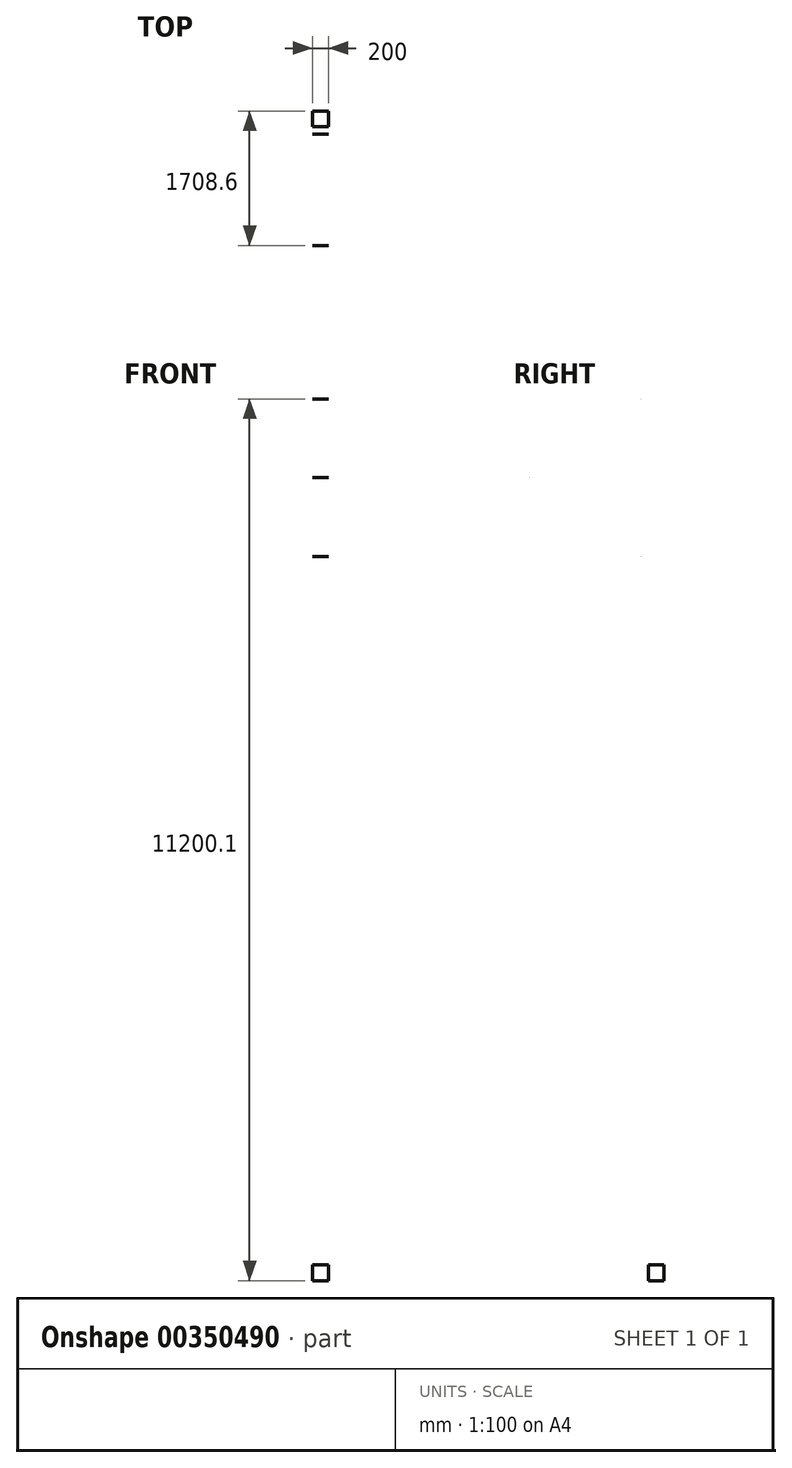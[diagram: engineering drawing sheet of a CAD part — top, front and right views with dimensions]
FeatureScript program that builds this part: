
annotation { "Feature Type Name" : "Feature", "Feature Type Description" : "" }
export const myFeature = defineFeature(function(context is Context, id is Id, definition is map)
    precondition{}
    {
        {
            var Q0;
            Q0=qCreatedBy(makeId("Right.planeOp"),FACE);
            var sketch = newSketch(context, id + "F0", { "sketchPlane" : qUnion([Q0])});
            skLineSegment(sketch, "E0", {"start": v(0, 0) * mm, "end": v(1000, 0) * mm});
            skLineSegment(sketch, "E1", {"start": v(1000, 0) * mm, "end": v(1000, 20000) * mm});
            skLineSegment(sketch, "E2", {"start": v(1000, 20000) * mm, "end": v(-1000, 20000) * mm});
            skLineSegment(sketch, "E3", {"start": v(-1000, 20000) * mm, "end": v(-1000, 0) * mm});
            skLineSegment(sketch, "E4", {"start": v(-1000, 0) * mm, "end": v(0, 0) * mm});
            skLineSegment(sketch, "E5", {"start": v(1000, 0) * mm, "end": v(800, 0) * mm});
            skLineSegment(sketch, "E6", {"start": v(800, 0) * mm, "end": v(800, 1141.07) * mm});
            skLineSegment(sketch, "E7", {"start": v(1000, 0) * mm, "end": v(1000, 200) * mm});
            skLineSegment(sketch, "E8", {"start": v(1000, 200) * mm, "end": v(-708.48, 200) * mm});
            skLineSegment(sketch, "E9", {"start": v(-1000, 0) * mm, "end": v(-800, 0) * mm});
            skLineSegment(sketch, "E10", {"start": v(-1000, 20000) * mm, "end": v(-1000, 19800) * mm});
            skLineSegment(sketch, "E11", {"start": v(800, 1141.07) * mm, "end": v(800, 200) * mm});
            skLineSegment(sketch, "E12", {"start": v(800, 1258.93) * mm, "end": v(800, 2150) * mm});
            skLineSegment(sketch, "E13", {"start": v(800, 2250) * mm, "end": v(800, 3141.07) * mm});
            skLineSegment(sketch, "E14", {"start": v(800, 3258.93) * mm, "end": v(800, 4150) * mm});
            skLineSegment(sketch, "E15", {"start": v(800, 4250) * mm, "end": v(800, 5141.07) * mm});
            skLineSegment(sketch, "E16", {"start": v(800, 5258.93) * mm, "end": v(800, 6150) * mm});
            skLineSegment(sketch, "E17", {"start": v(800, 6250) * mm, "end": v(800, 7141.07) * mm});
            skLineSegment(sketch, "E18", {"start": v(800, 7258.93) * mm, "end": v(800, 8150) * mm});
            skLineSegment(sketch, "E19", {"start": v(800, 8250) * mm, "end": v(800, 9141.07) * mm});
            skLineSegment(sketch, "E20", {"start": v(800, 9259) * mm, "end": v(800, 10150) * mm});
            skLineSegment(sketch, "E21", {"start": v(800, 10250) * mm, "end": v(800, 11141.14) * mm});
            skLineSegment(sketch, "E22", {"start": v(800, 11258.93) * mm, "end": v(800, 12150) * mm});
            skLineSegment(sketch, "E23", {"start": v(800, 12250) * mm, "end": v(800, 13141.07) * mm});
            skLineSegment(sketch, "E24", {"start": v(800, 13258.93) * mm, "end": v(800, 14150) * mm});
            skLineSegment(sketch, "E25", {"start": v(800, 14250) * mm, "end": v(800, 15141.07) * mm});
            skLineSegment(sketch, "E26", {"start": v(800, 15258.93) * mm, "end": v(800, 16150) * mm});
            skLineSegment(sketch, "E27", {"start": v(800, 16250) * mm, "end": v(800, 17141.07) * mm});
            skLineSegment(sketch, "E28", {"start": v(800, 17258.93) * mm, "end": v(800, 18150) * mm});
            skLineSegment(sketch, "E29", {"start": v(800, 18250) * mm, "end": v(800, 19141.07) * mm});
            skLineSegment(sketch, "E30", {"start": v(800, 19253.39) * mm, "end": v(800, 19800) * mm});
            skLineSegment(sketch, "E31", {"start": v(705.7, 9200) * mm, "end": v(705.4, 9200) * mm});
            skLineSegment(sketch, "E32", {"start": v(-708.6, 10204.1) * mm, "end": v(-708.37, 10204.1) * mm});
            skLineSegment(sketch, "E33", {"start": v(705.54, 11200) * mm, "end": v(705.24, 11200) * mm});
            skLineSegment(sketch, "E34", {"start": v(-803.08, 19800) * mm, "end": v(-802.95, 19800) * mm});
            skLineSegment(sketch, "E35.0.right", {"start": v(800, 19253.39) * mm, "end": v(-660.32, 19800) * mm});
            skArc(sketch, "E36.0.endCap", {"start": v(-802.95, 19150) * mm, "mid": v(-803.02, 19150) * mm, "end": v(-803.08, 19150) * mm});
            skArc(sketch, "E37.0.startCap", {"start": v(-802.95, 18150) * mm, "mid": v(-803.02, 18150) * mm, "end": v(-803.08, 18150) * mm});
            skLineSegment(sketch, "E37.0.left", {"start": v(-803.08, 18258.85) * mm, "end": v(625.39, 19150) * mm});
            skArc(sketch, "E37.1.endCap", {"start": v(-802.95, 18150) * mm, "mid": v(-803.02, 18150) * mm, "end": v(-803.08, 18150) * mm});
            skLineSegment(sketch, "E37.1.left", {"start": v(800, 18150) * mm, "end": v(-628.34, 18150) * mm});
            skLineSegment(sketch, "E37.1.right", {"start": v(800, 18250) * mm, "end": v(-628.34, 18250) * mm});
            skLineSegment(sketch, "E37.2.right", {"start": v(800, 17258.93) * mm, "end": v(-628.34, 18150) * mm});
            skArc(sketch, "E37.3.endCap", {"start": v(-802.95, 17150) * mm, "mid": v(-803.02, 17150) * mm, "end": v(-803.08, 17150) * mm});
            skArc(sketch, "E37.4.startCap", {"start": v(-802.95, 16150) * mm, "mid": v(-803.02, 16150) * mm, "end": v(-803.08, 16150) * mm});
            skLineSegment(sketch, "E37.4.left", {"start": v(-803.08, 16258.85) * mm, "end": v(625.39, 17150) * mm});
            skArc(sketch, "E37.5.endCap", {"start": v(-802.95, 16150) * mm, "mid": v(-803.02, 16150) * mm, "end": v(-803.08, 16150) * mm});
            skLineSegment(sketch, "E37.5.left", {"start": v(800, 16150) * mm, "end": v(-628.34, 16150) * mm});
            skLineSegment(sketch, "E37.5.right", {"start": v(800, 16250) * mm, "end": v(-628.34, 16250) * mm});
            skLineSegment(sketch, "E37.6.right", {"start": v(800, 15258.93) * mm, "end": v(-628.34, 16150) * mm});
            skArc(sketch, "E37.7.endCap", {"start": v(-802.95, 15150) * mm, "mid": v(-803.02, 15150) * mm, "end": v(-803.08, 15150) * mm});
            skArc(sketch, "E37.8.startCap", {"start": v(-802.95, 14150) * mm, "mid": v(-803.02, 14150) * mm, "end": v(-803.08, 14150) * mm});
            skLineSegment(sketch, "E37.8.left", {"start": v(-803.08, 14258.85) * mm, "end": v(625.39, 15150) * mm});
            skArc(sketch, "E37.9.endCap", {"start": v(-802.95, 14150) * mm, "mid": v(-803.02, 14150) * mm, "end": v(-803.08, 14150) * mm});
            skLineSegment(sketch, "E37.9.left", {"start": v(800, 14150) * mm, "end": v(-628.34, 14150) * mm});
            skLineSegment(sketch, "E37.9.right", {"start": v(800, 14250) * mm, "end": v(-628.34, 14250) * mm});
            skLineSegment(sketch, "E37.10.right", {"start": v(800, 13258.93) * mm, "end": v(-628.34, 14150) * mm});
            skArc(sketch, "E37.11.endCap", {"start": v(-802.95, 13150) * mm, "mid": v(-803.02, 13150) * mm, "end": v(-803.08, 13150) * mm});
            skArc(sketch, "E37.12.startCap", {"start": v(-802.95, 12150) * mm, "mid": v(-803.02, 12150) * mm, "end": v(-803.08, 12150) * mm});
            skLineSegment(sketch, "E37.12.left", {"start": v(-803.08, 12258.85) * mm, "end": v(625.39, 13150) * mm});
            skArc(sketch, "E37.13.endCap", {"start": v(-802.95, 12150) * mm, "mid": v(-803.02, 12150) * mm, "end": v(-803.08, 12150) * mm});
            skLineSegment(sketch, "E37.13.left", {"start": v(800, 12150) * mm, "end": v(-628.34, 12150) * mm});
            skLineSegment(sketch, "E37.13.right", {"start": v(800, 12250) * mm, "end": v(-628.34, 12250) * mm});
            skLineSegment(sketch, "E37.14.right", {"start": v(800, 11258.93) * mm, "end": v(-628.34, 12150) * mm});
            skArc(sketch, "E37.15.endCap", {"start": v(-802.95, 11150) * mm, "mid": v(-803.02, 11150) * mm, "end": v(-803.08, 11150) * mm});
            skLineSegment(sketch, "E37.16.left", {"start": v(-803.08, 10263.13) * mm, "end": v(624.74, 11150) * mm});
            skArc(sketch, "E37.17.endCap", {"start": v(800, 10150) * mm, "mid": v(799.93, 10150) * mm, "end": v(799.86, 10150) * mm});
            skLineSegment(sketch, "E37.17.right", {"start": v(-803.08, 10154.35) * mm, "end": v(-803.08, 10154.35) * mm});
            skLineSegment(sketch, "E37.18.right", {"start": v(800, 9259) * mm, "end": v(-628.22, 10153.88) * mm});
            skLineSegment(sketch, "E37.19.right", {"start": v(626.03, 9250) * mm, "end": v(-803.08, 9250) * mm});
            skLineSegment(sketch, "E37.20.left", {"start": v(-803.08, 8258.93) * mm, "end": v(625.25, 9150) * mm});
            skLineSegment(sketch, "E37.21.left", {"start": v(800, 8150) * mm, "end": v(-628.34, 8150) * mm});
            skLineSegment(sketch, "E37.21.right", {"start": v(800, 8250) * mm, "end": v(-628.34, 8250) * mm});
            skLineSegment(sketch, "E37.22.right", {"start": v(800, 7258.93) * mm, "end": v(-628.34, 8150) * mm});
            skLineSegment(sketch, "E37.23.left", {"start": v(625.25, 7150) * mm, "end": v(-803.08, 7150) * mm});
            skLineSegment(sketch, "E37.23.right", {"start": v(625.25, 7250) * mm, "end": v(-803.08, 7250) * mm});
            skLineSegment(sketch, "E37.24.left", {"start": v(-803.08, 6258.93) * mm, "end": v(625.25, 7150) * mm});
            skLineSegment(sketch, "E37.25.left", {"start": v(800, 6150) * mm, "end": v(-628.34, 6150) * mm});
            skLineSegment(sketch, "E37.25.right", {"start": v(800, 6250) * mm, "end": v(-628.34, 6250) * mm});
            skLineSegment(sketch, "E37.26.right", {"start": v(800, 5258.93) * mm, "end": v(-628.34, 6150) * mm});
            skLineSegment(sketch, "E37.28.left", {"start": v(-803.08, 4258.93) * mm, "end": v(625.25, 5150) * mm});
            skLineSegment(sketch, "E37.29.left", {"start": v(800, 4150) * mm, "end": v(-628.34, 4150) * mm});
            skLineSegment(sketch, "E37.29.right", {"start": v(800, 4250) * mm, "end": v(-628.34, 4250) * mm});
            skLineSegment(sketch, "E37.30.right", {"start": v(800, 3258.93) * mm, "end": v(-628.34, 4150) * mm});
            skLineSegment(sketch, "E37.31.right", {"start": v(625.25, 3250) * mm, "end": v(-803.08, 3250) * mm});
            skLineSegment(sketch, "E37.32.left", {"start": v(-803.08, 2258.93) * mm, "end": v(625.25, 3150) * mm});
            skLineSegment(sketch, "E37.33.left", {"start": v(800, 2150) * mm, "end": v(-628.34, 2150) * mm});
            skLineSegment(sketch, "E37.33.right", {"start": v(800, 2250) * mm, "end": v(-628.34, 2250) * mm});
            skLineSegment(sketch, "E37.34.right", {"start": v(800, 1258.93) * mm, "end": v(-628.34, 2150) * mm});
            skLineSegment(sketch, "E37.36.left", {"start": v(800, 1141.07) * mm, "end": v(-708.48, 200) * mm});
            skLineSegment(sketch, "E37.36.right", {"start": v(625.39, 1150) * mm, "end": v(-802.95, 258.93) * mm});
            skLineSegment(sketch, "E38.trimOffspring", {"start": v(625.25, 1250) * mm, "end": v(-803.08, 2141.07) * mm});
            skLineSegment(sketch, "E39.trimOffspring", {"start": v(625.25, 1250) * mm, "end": v(-803.08, 1250) * mm});
            skLineSegment(sketch, "E40.trimOffspring", {"start": v(625.39, 1150) * mm, "end": v(-802.95, 1150) * mm});
            skPoint(sketch, "E37.35.endCap.center.orphan", {"position": v(-803.08, 1200) * mm});
            skLineSegment(sketch, "E41.trimOffspring", {"start": v(-803.08, 1250) * mm, "end": v(-803.08, 2141.07) * mm});
            skLineSegment(sketch, "E42.trimOffspring", {"start": v(-802.95, 258.93) * mm, "end": v(-802.95, 1150) * mm});
            skPoint(sketch, "E43.orphan", {"position": v(-803.08, 200) * mm});
            skLineSegment(sketch, "E44.trimOffspring", {"start": v(-628.34, 2250) * mm, "end": v(800, 3141.07) * mm});
            skLineSegment(sketch, "E45.trimOffspring", {"start": v(-803.08, 2258.93) * mm, "end": v(-803.08, 3150) * mm});
            skPoint(sketch, "E37.33.endCap.center.orphan", {"position": v(-803.08, 2200) * mm});
            skLineSegment(sketch, "E46.trimOffspring", {"start": v(625.25, 3150) * mm, "end": v(-803.08, 3150) * mm});
            skLineSegment(sketch, "E47.trimOffspring", {"start": v(625.25, 3250) * mm, "end": v(-803.08, 4141.07) * mm});
            skPoint(sketch, "E37.31.endCap.center.orphan", {"position": v(-803.08, 3200) * mm});
            skLineSegment(sketch, "E48.trimOffspring", {"start": v(-803.08, 3250) * mm, "end": v(-803.08, 4141.07) * mm});
            skLineSegment(sketch, "E49.trimOffspring", {"start": v(-628.34, 4250) * mm, "end": v(800, 5141.07) * mm});
            skLineSegment(sketch, "E50.trimOffspring", {"start": v(-803.08, 4258.93) * mm, "end": v(-803.08, 5150) * mm});
            skPoint(sketch, "E37.30.endCap.center.orphan", {"position": v(-803.08, 4200) * mm});
            skLineSegment(sketch, "E51.trimOffspring", {"start": v(-803.08, 5250) * mm, "end": v(-803.08, 6141.07) * mm});
            skLineSegment(sketch, "E52.trimOffspring", {"start": v(625.25, 5250) * mm, "end": v(-803.08, 6141.07) * mm});
            skLineSegment(sketch, "E53.trimOffspring", {"start": v(625.25, 5250) * mm, "end": v(-803.08, 5250) * mm});
            skLineSegment(sketch, "E54.trimOffspring", {"start": v(625.25, 5150) * mm, "end": v(-803.08, 5150) * mm});
            skPoint(sketch, "E37.23.endCap.center.orphan", {"position": v(-803.08, 7200) * mm});
            skLineSegment(sketch, "E55.trimOffspring", {"start": v(-803.08, 7250) * mm, "end": v(-803.08, 8141.07) * mm});
            skLineSegment(sketch, "E56.trimOffspring", {"start": v(-628.34, 6250) * mm, "end": v(800, 7141.07) * mm});
            skLineSegment(sketch, "E57.trimOffspring", {"start": v(-803.08, 6258.93) * mm, "end": v(-803.08, 7150) * mm});
            skLineSegment(sketch, "E58.trimOffspring", {"start": v(625.25, 7250) * mm, "end": v(-803.08, 8141.07) * mm});
            skLineSegment(sketch, "E59.trimOffspring", {"start": v(-628.34, 8250) * mm, "end": v(800, 9141.07) * mm});
            skLineSegment(sketch, "E60.trimOffspring", {"start": v(-803.08, 8258.93) * mm, "end": v(-803.08, 9150) * mm});
            skPoint(sketch, "E37.20.startCap.center.orphan", {"position": v(-803.08, 8200) * mm});
            skPoint(sketch, "E37.19.endCap.center.orphan", {"position": v(-803.08, 9200) * mm});
            skLineSegment(sketch, "E61.trimOffspring", {"start": v(-803.08, 9250) * mm, "end": v(-803.08, 10145.43) * mm});
            skLineSegment(sketch, "E62.trimOffspring", {"start": v(626.03, 9250) * mm, "end": v(-803.08, 10145.43) * mm});
            skLineSegment(sketch, "E63.trimOffspring", {"start": v(705.4, 9200) * mm, "end": v(705.55, 9200.1) * mm});
            skLineSegment(sketch, "E64.trimOffspring", {"start": v(625.25, 9150) * mm, "end": v(-803.08, 9150) * mm});
            skLineSegment(sketch, "E65.trimOffspring", {"start": v(705.7, 9200) * mm, "end": v(705.55, 9200.1) * mm});
            skLineSegment(sketch, "E66.trimOffspring", {"start": v(-628.45, 10253.88) * mm, "end": v(800.14, 10250) * mm});
            skLineSegment(sketch, "E67.trimOffspring", {"start": v(-628.45, 10253.88) * mm, "end": v(800, 11141.14) * mm});
            skLineSegment(sketch, "E68.trimOffspring", {"start": v(-708.37, 10204.1) * mm, "end": v(-708.48, 10204.17) * mm});
            skLineSegment(sketch, "E69.trimOffspring", {"start": v(-628.22, 10153.88) * mm, "end": v(799.86, 10150) * mm});
            skLineSegment(sketch, "E70.trimOffspring", {"start": v(-708.6, 10204.1) * mm, "end": v(-708.48, 10204.17) * mm});
            skArc(sketch, "E71.trimOffspring", {"start": v(-803.08, 10254.35) * mm, "mid": v(-802.95, 10254.35) * mm, "end": v(-802.81, 10254.35) * mm});
            skLineSegment(sketch, "E72.trimOffspring", {"start": v(-803.08, 10263.13) * mm, "end": v(-803.08, 11150) * mm});
            skArc(sketch, "E73.trimOffspring", {"start": v(-803.08, 11250) * mm, "mid": v(-803.02, 11250) * mm, "end": v(-802.95, 11250) * mm});
            skLineSegment(sketch, "E74.trimOffspring", {"start": v(-803.08, 11250) * mm, "end": v(-803.08, 12141.15) * mm});
            skLineSegment(sketch, "E75.trimOffspring", {"start": v(625.39, 11250) * mm, "end": v(-802.95, 11250) * mm});
            skLineSegment(sketch, "E76.trimOffspring", {"start": v(625.39, 11250) * mm, "end": v(-803.08, 12141.15) * mm});
            skLineSegment(sketch, "E77.trimOffspring", {"start": v(705.24, 11200) * mm, "end": v(705.39, 11200.1) * mm});
            skLineSegment(sketch, "E78.trimOffspring", {"start": v(624.74, 11150) * mm, "end": v(-802.95, 11150) * mm});
            skLineSegment(sketch, "E79.trimOffspring", {"start": v(705.54, 11200) * mm, "end": v(705.39, 11200.1) * mm});
            skLineSegment(sketch, "E80.trimOffspring", {"start": v(-628.34, 12250) * mm, "end": v(800, 13141.07) * mm});
            skLineSegment(sketch, "E81.trimOffspring", {"start": v(-803.08, 12258.85) * mm, "end": v(-803.08, 13150) * mm});
            skArc(sketch, "E82.trimOffspring", {"start": v(-803.08, 12250) * mm, "mid": v(-803.02, 12250) * mm, "end": v(-802.95, 12250) * mm});
            skArc(sketch, "E83.trimOffspring", {"start": v(-803.08, 13250) * mm, "mid": v(-803.02, 13250) * mm, "end": v(-802.95, 13250) * mm});
            skLineSegment(sketch, "E84.trimOffspring", {"start": v(-803.08, 13250) * mm, "end": v(-803.08, 14141.15) * mm});
            skLineSegment(sketch, "E85.trimOffspring", {"start": v(625.39, 13250) * mm, "end": v(-802.95, 13250) * mm});
            skLineSegment(sketch, "E86.trimOffspring", {"start": v(625.39, 13250) * mm, "end": v(-803.08, 14141.15) * mm});
            skLineSegment(sketch, "E87.trimOffspring", {"start": v(625.39, 13150) * mm, "end": v(-802.95, 13150) * mm});
            skLineSegment(sketch, "E88.trimOffspring", {"start": v(-628.34, 14250) * mm, "end": v(800, 15141.07) * mm});
            skLineSegment(sketch, "E89.trimOffspring", {"start": v(-803.08, 14258.85) * mm, "end": v(-803.08, 15150) * mm});
            skArc(sketch, "E90.trimOffspring", {"start": v(-803.08, 14250) * mm, "mid": v(-803.02, 14250) * mm, "end": v(-802.95, 14250) * mm});
            skArc(sketch, "E91.trimOffspring", {"start": v(-803.08, 15250) * mm, "mid": v(-803.02, 15250) * mm, "end": v(-802.95, 15250) * mm});
            skLineSegment(sketch, "E92.trimOffspring", {"start": v(800, 16200) * mm, "end": v(800, 17141.07) * mm});
            skLineSegment(sketch, "E93.trimOffspring", {"start": v(-803.08, 15250) * mm, "end": v(-803.08, 16141.15) * mm});
            skLineSegment(sketch, "E94.trimOffspring", {"start": v(625.39, 15250) * mm, "end": v(-803.08, 16141.15) * mm});
            skLineSegment(sketch, "E95.trimOffspring", {"start": v(625.39, 15250) * mm, "end": v(-802.95, 15250) * mm});
            skLineSegment(sketch, "E96.trimOffspring", {"start": v(625.39, 15150) * mm, "end": v(-802.95, 15150) * mm});
            skLineSegment(sketch, "E97.trimOffspring", {"start": v(-628.34, 16250) * mm, "end": v(800, 17141.07) * mm});
            skLineSegment(sketch, "E98.trimOffspring", {"start": v(-803.08, 16258.85) * mm, "end": v(-803.08, 17150) * mm});
            skArc(sketch, "E99.trimOffspring", {"start": v(-803.08, 16250) * mm, "mid": v(-803.02, 16250) * mm, "end": v(-802.95, 16250) * mm});
            skArc(sketch, "E100.trimOffspring", {"start": v(-803.08, 17250) * mm, "mid": v(-803.02, 17250) * mm, "end": v(-802.95, 17250) * mm});
            skLineSegment(sketch, "E101.trimOffspring", {"start": v(-803.08, 17250) * mm, "end": v(-803.08, 18141.15) * mm});
            skLineSegment(sketch, "E102.trimOffspring", {"start": v(625.39, 17250) * mm, "end": v(-802.95, 17250) * mm});
            skLineSegment(sketch, "E103.trimOffspring", {"start": v(625.39, 17250) * mm, "end": v(-803.08, 18141.15) * mm});
            skLineSegment(sketch, "E104.trimOffspring", {"start": v(625.39, 17150) * mm, "end": v(-802.95, 17150) * mm});
            skLineSegment(sketch, "E105.trimOffspring", {"start": v(-628.34, 18250) * mm, "end": v(800, 19141.07) * mm});
            skLineSegment(sketch, "E106.trimOffspring", {"start": v(-803.08, 18258.85) * mm, "end": v(-803.08, 19150) * mm});
            skArc(sketch, "E107.trimOffspring", {"start": v(-803.08, 18250) * mm, "mid": v(-803.02, 18250) * mm, "end": v(-802.95, 18250) * mm});
            skLineSegment(sketch, "E108.trimOffspring", {"start": v(-803.08, 20000) * mm, "end": v(-803.08, 20001.85) * mm});
            skArc(sketch, "E109.trimOffspring", {"start": v(-803.08, 19250) * mm, "mid": v(-803.02, 19250) * mm, "end": v(-802.95, 19250) * mm});
            skLineSegment(sketch, "E110.trimOffspring", {"start": v(-803.08, 19250) * mm, "end": v(-803.08, 19746.66) * mm});
            skPoint(sketch, "E35.0.endCap.center.orphan", {"position": v(-802.95, 19800) * mm});
            skLineSegment(sketch, "E111.trimOffspring", {"start": v(-660.32, 19800) * mm, "end": v(800, 19800) * mm});
            skLineSegment(sketch, "E112.trimOffspring", {"start": v(523.8, 19250) * mm, "end": v(-802.95, 19250) * mm});
            skLineSegment(sketch, "E113.trimOffspring", {"start": v(523.8, 19250) * mm, "end": v(-803.08, 19746.66) * mm});
            skLineSegment(sketch, "E114.trimOffspring", {"start": v(625.39, 19150) * mm, "end": v(-802.95, 19150) * mm});
            skSolve(sketch);
        }
        {
            var Q0;
            Q0=makeQuery(id+"F0.imprint","IMPRINT",FACE,{"disambiguationData":[TD([[makeQuery(id+"F0.imprint","IMPRINT",EDGE,{"derivedFrom":sQuery(id+"F0.wireOp",EDGE,"E5")}),-1.0]])]});
            var Q1;
            Q1=makeQuery(id+"F0.imprint","IMPRINT",FACE,{"disambiguationData":[TD([[makeQuery(id+"F0.imprint","IMPRINT",EDGE,{"derivedFrom":sQuery(id+"F0.wireOp",EDGE,"E31")}),-1.0]])]});
            var Q2;
            Q2=makeQuery(id+"F0.imprint","IMPRINT",FACE,{"disambiguationData":[TD([[makeQuery(id+"F0.imprint","IMPRINT",EDGE,{"derivedFrom":sQuery(id+"F0.wireOp",EDGE,"E33")}),-1.0]])]});
            var Q3;
            Q3=makeQuery(id+"F0.imprint","IMPRINT",FACE,{"disambiguationData":[TD([[makeQuery(id+"F0.imprint","IMPRINT",EDGE,{"derivedFrom":sQuery(id+"F0.wireOp",EDGE,"E32")}),1.0]])]});
            var Q4;
            Q4=makeQuery(id+"F0.imprint","IMPRINT",FACE,{"disambiguationData":[TD([[makeQuery(id+"F0.imprint","IMPRINT",EDGE,{"derivedFrom":sQuery(id+"F0.wireOp",EDGE,"E0")}),1.0]])]});
            extrude(context, id + "F1", {"entities" : qUnion([Q0, Q1, Q2, Q3, Q4]), "depth" : 200 * mm});
        }
    });
